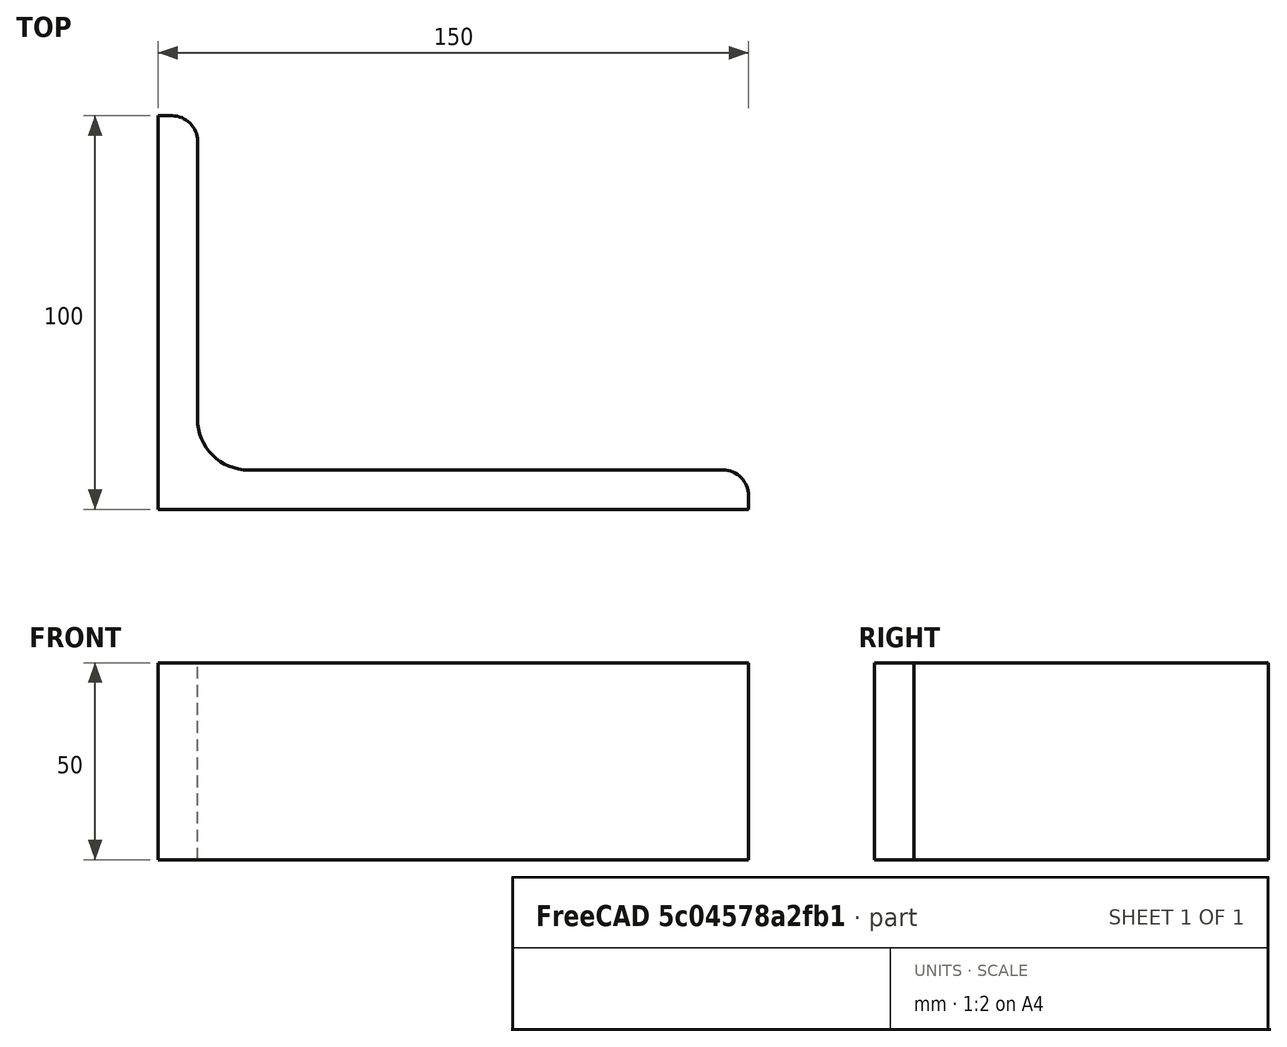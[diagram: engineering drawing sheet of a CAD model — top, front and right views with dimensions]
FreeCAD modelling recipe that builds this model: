
FCSTD DOCUMENT  (FreeCAD 0.15R4671 (Git))
Label: Angle Bar 150x100x10 EN10056 S235JR
License: All rights reserved
LicenseURL: http://en.wikipedia.org/wiki/All_rights_reserved
objects: Sketcher::SketchObject×1, Part::Extrusion×1
note: 2 computed .brp shape members not serialized (recipe doc carries the construction recipe); baked Part::Feature solids carry a one-line shape summary decoded from their .brp

FEATURE [Sketcher::SketchObject] Sketch
  sketch-geometry (9):
    g0: LineSegment StartX=0 StartY=0 StartZ=0 EndX=150 EndY=0 EndZ=0
    g1: LineSegment StartX=150 StartY=0 StartZ=0 EndX=150 EndY=3.5 EndZ=0
    g2: LineSegment StartX=143.5 StartY=10 StartZ=0 EndX=23 EndY=10 EndZ=0
    g3: LineSegment StartX=0 StartY=0 StartZ=0 EndX=0 EndY=100 EndZ=0
    g4: LineSegment StartX=0 StartY=100 StartZ=0 EndX=3.5 EndY=100 EndZ=0
    g5: LineSegment StartX=10 StartY=93.5 StartZ=0 EndX=10 EndY=23 EndZ=0
    g6: ArcOfCircle CenterX=23 CenterY=23 CenterZ=0 NormalX=0 NormalY=0 NormalZ=1 Radius=13 StartAngle=3.14159 EndAngle=4.71239
    g7: ArcOfCircle CenterX=3.5 CenterY=93.5 CenterZ=0 NormalX=0 NormalY=0 NormalZ=1 Radius=6.5 StartAngle=0 EndAngle=1.5708
    g8: ArcOfCircle CenterX=143.5 CenterY=3.5 CenterZ=0 NormalX=0 NormalY=0 NormalZ=1 Radius=6.5 StartAngle=0 EndAngle=1.5708
  constraints (23):
    c: Coincident(g0,g-1)
    c: Horizontal(g0)
    c: Coincident(g1,g0)
    c: Vertical(g1)
    c: Horizontal(g2)
    c: Coincident(g3,g-1)
    c: Vertical(g3)
    c: Coincident(g4,g3)
    c: Horizontal(g4)
    c: Vertical(g5)
    c: Tangent(g5,g6) = -1.5708
    c: Tangent(g2,g6) = 1.5708
    c: Tangent(g4,g7) = 1.5708
    c: Tangent(g5,g7) = 1.5708
    c: Tangent(g2,g8) = -1.5708
    c: Tangent(g1,g8) = -1.5708
    c: DistanceX(g0) = 150
    c: DistanceY(g3) = 100
    c: DistanceY(g0,g2) = 10
    c: DistanceX(g3,g5) = 10
    c: Radius(g6) = 13
    c: Radius(g8) = 6.5
    c: Radius(g7) = 6.5
FEATURE [Part::Extrusion] Extrude  label="Angle Bar 150x100x10 EN10056 S235JR"
  Base = -> Sketch
  Dir = (0,0,50)
  Solid = true
